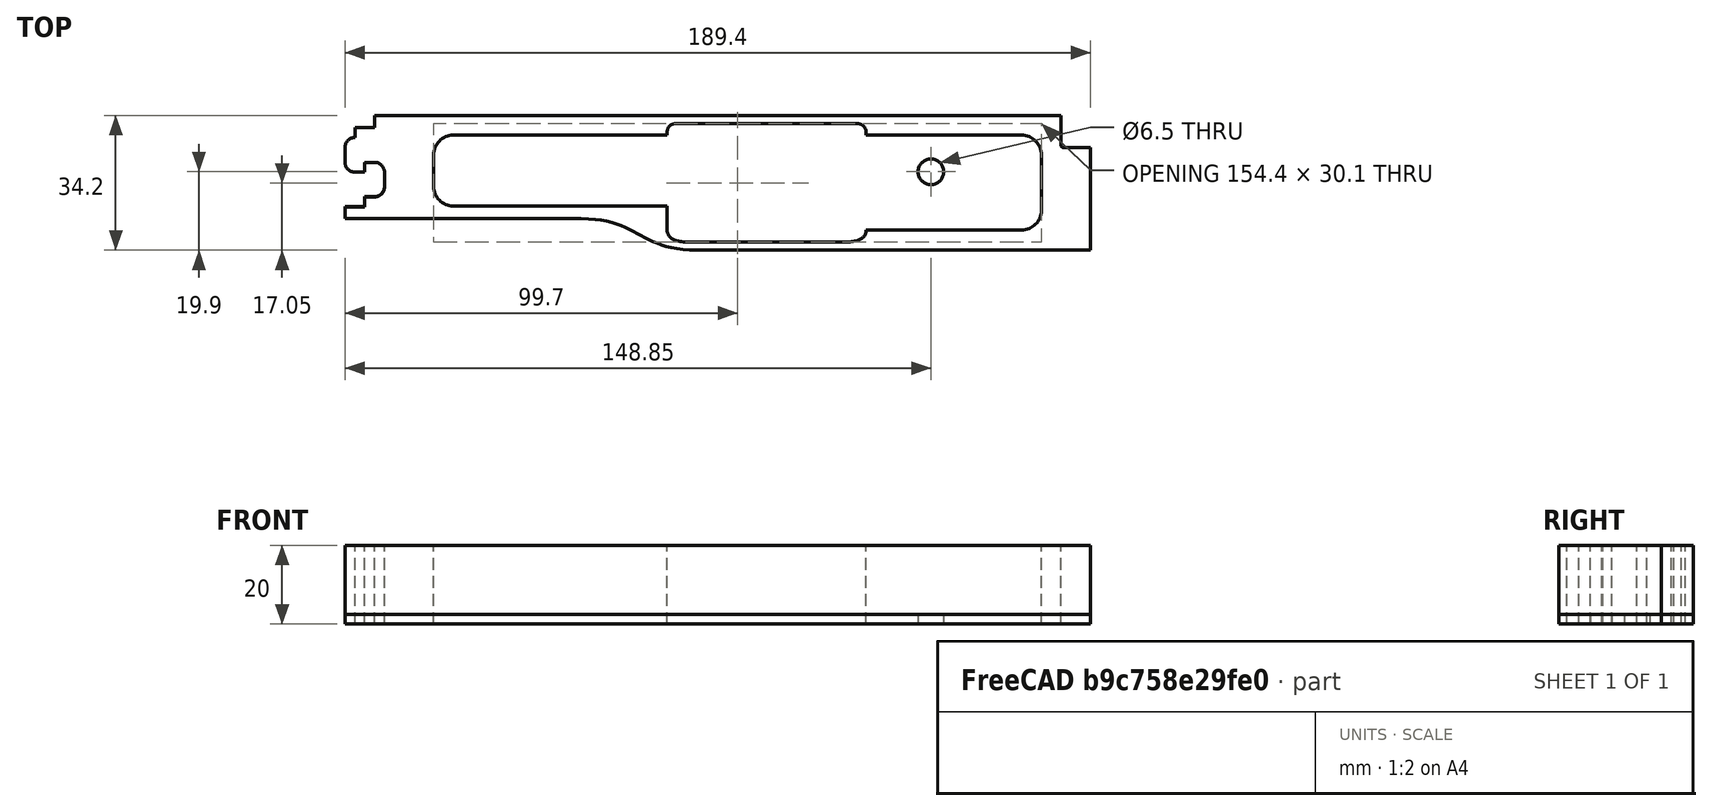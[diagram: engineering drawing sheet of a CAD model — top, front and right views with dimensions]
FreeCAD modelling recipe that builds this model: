
FCSTD DOCUMENT  (FreeCAD 0.19R0.19.2)
Label: v0_29
License: All rights reserved
LicenseURL: http://en.wikipedia.org/wiki/All_rights_reserved
objects: Sketcher::SketchObject×2, Part::Extrusion×2
note: 4 computed .brp shape members not serialized (recipe doc carries the construction recipe); baked Part::Feature solids carry a one-line shape summary decoded from their .brp

FEATURE [Sketcher::SketchObject] Sketch
  FullyConstrained = true
  sketch-geometry (35):
    g0: LineSegment StartX=0 StartY=0 StartZ=0 EndX=154.4 EndY=0 EndZ=0
    g1: LineSegment StartX=154.4 StartY=0 StartZ=0 EndX=154.4 EndY=-7.6 EndZ=0
    g2: ArcOfCircle CenterX=154.9 CenterY=-7.6 CenterZ=0 NormalX=0 NormalY=0 NormalZ=1 AngleXU=0 Radius=0.5 StartAngle=3.14159 EndAngle=4.71239
    g3: LineSegment StartX=32.5209 StartY=-26.2 StartZ=0 EndX=-7.5 EndY=-26.2 EndZ=0
    g4: LineSegment StartX=61.85 StartY=-34.2 StartZ=0 EndX=161.9 EndY=-34.2 EndZ=0
    g5: LineSegment StartX=161.9 StartY=-8.1 StartZ=0 EndX=161.9 EndY=-34.2 EndZ=0
    g6: LineSegment StartX=154.9 StartY=-8.1 StartZ=0 EndX=161.9 EndY=-8.1 EndZ=0
    g7-g11: Circle x5 (B-spline internal-alignment scaffolding for g12; pole/knot coordinates omitted)
    g12: BSplineCurve PolesCount=5 KnotsCount=3 Degree=3 IsPeriodic=0
    g13: GeomPoint X=61.85 Y=-34.2 Z=0
    g14: GeomPoint X=47.185 Y=-30.2 Z=0
    g15: GeomPoint X=32.5209 Y=-26.2 Z=0
    g16: Circle CenterX=121.35 CenterY=-14.3 CenterZ=0 NormalX=0 NormalY=0 NormalZ=1 AngleXU=0 Radius=3.25
    g17: LineSegment StartX=-7.5 StartY=-26.2 StartZ=0 EndX=-27.5 EndY=-26.2 EndZ=0
    g18: LineSegment StartX=-20 StartY=0 StartZ=0 EndX=0 EndY=0 EndZ=0
    g19: LineSegment StartX=-25 StartY=-3.1 StartZ=0 EndX=-20 EndY=-3.1 EndZ=0
    g20: LineSegment StartX=-25 StartY=-3.1 StartZ=0 EndX=-25 EndY=-5.6 EndZ=0
    g21: LineSegment StartX=-27.5 StartY=-8.1 StartZ=0 EndX=-27.5 EndY=-11.85 EndZ=0
    g22: ArcOfCircle CenterX=-25 CenterY=-8.1 CenterZ=0 NormalX=0 NormalY=0 NormalZ=1 AngleXU=0 Radius=2.5 StartAngle=1.5708 EndAngle=3.14159
    g23: LineSegment StartX=-25 StartY=-14.35 StartZ=0 EndX=-22.5 EndY=-14.35 EndZ=0
    g24: ArcOfCircle CenterX=-25 CenterY=-11.85 CenterZ=0 NormalX=0 NormalY=0 NormalZ=1 AngleXU=0 Radius=2.5 StartAngle=3.14159 EndAngle=4.71239
    g25: LineSegment StartX=-22.5 StartY=-14.35 StartZ=0 EndX=-22.5 EndY=-11.85 EndZ=0
    g26: LineSegment StartX=-22.5 StartY=-11.85 StartZ=0 EndX=-20 EndY=-11.85 EndZ=0
    g27: ArcOfCircle CenterX=-20 CenterY=-14.35 CenterZ=0 NormalX=0 NormalY=0 NormalZ=1 AngleXU=0 Radius=2.5 StartAngle=8e-16 EndAngle=1.5708
    g28: LineSegment StartX=-17.5 StartY=-14.35 StartZ=0 EndX=-17.5 EndY=-18.1 EndZ=0
    g29: ArcOfCircle CenterX=-20 CenterY=-18.1 CenterZ=0 NormalX=0 NormalY=0 NormalZ=1 AngleXU=0 Radius=2.5 StartAngle=4.71239 EndAngle=6.28319
    g30: LineSegment StartX=-22.5 StartY=-20.6 StartZ=0 EndX=-20 EndY=-20.6 EndZ=0
    g31: LineSegment StartX=-22.5 StartY=-20.6 StartZ=0 EndX=-22.5 EndY=-23.1 EndZ=0
    g32: LineSegment StartX=-27.5 StartY=-23.1 StartZ=0 EndX=-22.5 EndY=-23.1 EndZ=0
    g33: LineSegment StartX=-20 StartY=-3.1 StartZ=0 EndX=-20 EndY=0 EndZ=0
    g34: LineSegment StartX=-27.5 StartY=-23.1 StartZ=0 EndX=-27.5 EndY=-26.2 EndZ=0
  constraints (70):
    c: PointOnObject(g0,g-2)
    c: Horizontal(g0)
    c: Distance(g0) = 154.4
    c: DistanceY(g-1,g0) = 0
    c: Vertical(g1)
    c: Distance(g1) = 7.6
    c: Coincident(g1,g0)
    c: Block(g2)
    c: Horizontal(g4)
    c: Horizontal(g3)
    c: Block(g3)
    c: Block(g4)
    c: Vertical(g5)
    c: Distance(g5) = 26.1
    c: Coincident(g5,g4)
    c: Horizontal(g6)
    c: Coincident(g6,g5)
    c: Coincident(g6,g2)
    c: Distance(g6) = 7
    c: Coincident(g12,g4)
    c: Weight(g7) = 1
    c: Equal(g7, g8-g11) x4
    c: Coincident(g12,g3)
    c: InternalAlignment(g7-g11 -> g12) x5
    c: InternalAlignment(g13,g12)
    c: InternalAlignment(g14,g12)
    c: InternalAlignment(g15,g12)
    c: Block(g12)
    c: Block(g16)
    c: Coincident(g17,g3)
    c: Horizontal(g17)
    c: Distance(g17) = 20
    c: Horizontal(g18)
    c: Distance(g18) = 20
    c: Coincident(g18,g0)
    c: Horizontal(g19)
    c: Vertical(g20)
    c: Coincident(g20,g19)
    c: Vertical(g21)
    c: Coincident(g22,g20)
    c: Block(g22)
    c: Coincident(g21,g22)
    c: Horizontal(g23)
    c: Coincident(g24,g21)
    c: Block(g24)
    c: Block(g23)
    c: Vertical(g25)
    c: Coincident(g25,g23)
    c: Horizontal(g26)
    c: Coincident(g26,g25)
    c: Coincident(g27,g26)
    c: Vertical(g28)
    c: Block(g27)
    c: Coincident(g28,g27)
    c: Coincident(g29,g28)
    c: Block(g29)
    c: Horizontal(g30)
    c: Coincident(g30,g29)
    c: Vertical(g31)
    c: Coincident(g31,g30)
    c: Horizontal(g32)
    c: Coincident(g32,g31)
    c: Block(g19)
    c: Block(g32)
    c: Coincident(g33,g19)
    c: Coincident(g33,g18)
    c: Vertical(g33)
    c: Coincident(g34,g32)
    c: Coincident(g34,g17)
    c: Vertical(g34)
FEATURE [Part::Extrusion] Extrude
  Base = -> Sketch
  Dir = (0,0,1)
  DirMode = 2
  FaceMakerClass = Part::FaceMakerBullseye
  LengthFwd = 2.4
  LengthRev = 0
  Solid = true
  Symmetric = false
FEATURE [Sketcher::SketchObject] Sketch001
  FullyConstrained = true
  sketch-geometry (65):
    g0: ArcOfCircle CenterX=144.4 CenterY=-10 CenterZ=0 NormalX=0 NormalY=0 NormalZ=1 AngleXU=0 Radius=5 StartAngle=0 EndAngle=1.5708
    g1: LineSegment StartX=32.5209 StartY=-26.2 StartZ=0 EndX=-7.49911 EndY=-26.2 EndZ=0
    g2: LineSegment StartX=61.85 StartY=-34.2 StartZ=0 EndX=161.9 EndY=-34.2 EndZ=0
    g3: ArcOfCircle CenterX=144.4 CenterY=-24.1 CenterZ=0 NormalX=0 NormalY=0 NormalZ=1 AngleXU=0 Radius=5 StartAngle=4.71239 EndAngle=6.28319
    g4: Circle CenterX=104.85 CenterY=-29.2 CenterZ=0 NormalX=0 NormalY=0 NormalZ=1 AngleXU=0 Radius=1
    g5: Circle CenterX=104.85 CenterY=-32.2 CenterZ=0 NormalX=0 NormalY=0 NormalZ=1 AngleXU=0 Radius=1
    g6: Circle CenterX=98.85 CenterY=-32.2 CenterZ=0 NormalX=0 NormalY=0 NormalZ=1 AngleXU=0 Radius=1
    g7: BSplineCurve PolesCount=3 KnotsCount=2 Degree=2 IsPeriodic=0
    g8: GeomPoint X=104.85 Y=-29.2 Z=0
    g9: GeomPoint X=98.85 Y=-32.2 Z=0
    g10: Circle CenterX=54.35 CenterY=-29.2 CenterZ=0 NormalX=0 NormalY=0 NormalZ=1 AngleXU=0 Radius=1
    g11: Circle CenterX=60.35 CenterY=-32.2 CenterZ=0 NormalX=0 NormalY=0 NormalZ=1 AngleXU=0 Radius=1
    g12: BSplineCurve PolesCount=3 KnotsCount=2 Degree=2 IsPeriodic=0
    g13: GeomPoint X=54.35 Y=-29.2 Z=0
    g14: GeomPoint X=60.35 Y=-32.2 Z=0
    g15: ArcOfCircle CenterX=56.35 CenterY=-4.1 CenterZ=0 NormalX=0 NormalY=0 NormalZ=1 AngleXU=0 Radius=2 StartAngle=1.5708 EndAngle=3.14159
    g16: ArcOfCircle CenterX=102.85 CenterY=-4.1 CenterZ=0 NormalX=0 NormalY=0 NormalZ=1 AngleXU=0 Radius=2 StartAngle=1e-16 EndAngle=1.5708
    g17: LineSegment StartX=0 StartY=0 StartZ=0 EndX=154.4 EndY=0 EndZ=0
    g18: ArcOfCircle CenterX=154.9 CenterY=-7.6 CenterZ=0 NormalX=0 NormalY=0 NormalZ=1 AngleXU=0 Radius=0.5 StartAngle=3.14159 EndAngle=4.71239
    g19-g23: Circle x5 (B-spline internal-alignment scaffolding for g24; pole/knot coordinates omitted)
    g24: BSplineCurve PolesCount=5 KnotsCount=3 Degree=3 IsPeriodic=0
    g25: GeomPoint X=61.85 Y=-34.2 Z=0
    g26: GeomPoint X=47.1857 Y=-30.2 Z=0
    g27: GeomPoint X=32.5209 Y=-26.2 Z=0
    g28: LineSegment StartX=154.4 StartY=0 StartZ=0 EndX=154.4 EndY=-7.6 EndZ=0
    g29: LineSegment StartX=154.9 StartY=-8.1 StartZ=0 EndX=161.9 EndY=-8.1 EndZ=0
    g30: LineSegment StartX=161.9 StartY=-8.1 StartZ=0 EndX=161.9 EndY=-34.2 EndZ=0
    g31: LineSegment StartX=20 StartY=-5 StartZ=0 EndX=54.35 EndY=-5 EndZ=0
    g32: LineSegment StartX=54.35 StartY=-5 StartZ=0 EndX=54.35 EndY=-4.1 EndZ=0
    g33: LineSegment StartX=56.35 StartY=-2.1 StartZ=0 EndX=102.85 EndY=-2.1 EndZ=0
    g34: LineSegment StartX=104.85 StartY=-4.1 StartZ=0 EndX=104.85 EndY=-5 EndZ=0
    g35: LineSegment StartX=104.85 StartY=-5 StartZ=0 EndX=144.4 EndY=-5 EndZ=0
    g36: LineSegment StartX=149.4 StartY=-10 StartZ=0 EndX=149.4 EndY=-24.1 EndZ=0
    g37: LineSegment StartX=144.4 StartY=-29.1 StartZ=0 EndX=104.85 EndY=-29.1 EndZ=0
    g38: LineSegment StartX=104.85 StartY=-29.1 StartZ=0 EndX=104.85 EndY=-29.2 EndZ=0
    g39: LineSegment StartX=98.85 StartY=-32.2 StartZ=0 EndX=60.35 EndY=-32.2 EndZ=0
    g40: LineSegment StartX=54.35 StartY=-29.2 StartZ=0 EndX=54.35 EndY=-23 EndZ=0
    g41: LineSegment StartX=54.35 StartY=-23 StartZ=0 EndX=20 EndY=-23 EndZ=0
    g42: LineSegment StartX=-27.4991 StartY=-26.2 StartZ=0 EndX=-7.49911 EndY=-26.2 EndZ=0
    g43: LineSegment StartX=-20 StartY=0 StartZ=0 EndX=0 EndY=0 EndZ=0
    g44: LineSegment StartX=-27.4991 StartY=-23.2 StartZ=0 EndX=-22.5 EndY=-23.2 EndZ=0
    g45: LineSegment StartX=-22.5 StartY=-20.7 StartZ=0 EndX=-22.5 EndY=-23.2 EndZ=0
    g46: LineSegment StartX=-22.5 StartY=-20.7 StartZ=0 EndX=-20 EndY=-20.7 EndZ=0
    g47: ArcOfCircle CenterX=-20 CenterY=-18.2 CenterZ=0 NormalX=0 NormalY=0 NormalZ=1 AngleXU=0 Radius=2.5 StartAngle=4.71239 EndAngle=6.28319
    g48: LineSegment StartX=-17.5 StartY=-14.4 StartZ=0 EndX=-17.5 EndY=-18.2 EndZ=0
    g49: ArcOfCircle CenterX=-20 CenterY=-14.4 CenterZ=0 NormalX=0 NormalY=0 NormalZ=1 AngleXU=0 Radius=2.5 StartAngle=9e-16 EndAngle=1.5708
    g50: LineSegment StartX=-22.5 StartY=-11.9 StartZ=0 EndX=-20 EndY=-11.9 EndZ=0
    g51: LineSegment StartX=-22.5 StartY=-14.4 StartZ=0 EndX=-22.5 EndY=-11.9 EndZ=0
    g52: LineSegment StartX=-25 StartY=-14.4 StartZ=0 EndX=-22.5 EndY=-14.4 EndZ=0
    g53: ArcOfCircle CenterX=-25 CenterY=-11.9 CenterZ=0 NormalX=0 NormalY=0 NormalZ=1 AngleXU=0 Radius=2.5 StartAngle=3.14159 EndAngle=4.71239
    g54: LineSegment StartX=-27.5 StartY=-8.1 StartZ=0 EndX=-27.5 EndY=-11.9 EndZ=0
    g55: ArcOfCircle CenterX=-25 CenterY=-8.1 CenterZ=0 NormalX=0 NormalY=0 NormalZ=1 AngleXU=0 Radius=2.5 StartAngle=1.5708 EndAngle=3.14159
    g56: LineSegment StartX=-25 StartY=-3.1 StartZ=0 EndX=-25 EndY=-5.6 EndZ=0
    g57: LineSegment StartX=-20 StartY=-3.1 StartZ=0 EndX=-25 EndY=-3.1 EndZ=0
    g58: LineSegment StartX=-20 StartY=0 StartZ=0 EndX=-20 EndY=-3.1 EndZ=0
    g59: LineSegment StartX=-27.4991 StartY=-26.2 StartZ=0 EndX=-27.4991 EndY=-23.2 EndZ=0
    g60: LineSegment StartX=4.09e-14 StartY=-5 StartZ=0 EndX=20 EndY=-5 EndZ=0
    g61: ArcOfCircle CenterX=7.1e-15 CenterY=-18 CenterZ=0 NormalX=0 NormalY=0 NormalZ=1 AngleXU=0 Radius=5 StartAngle=3.14159 EndAngle=4.71239
    g62: ArcOfCircle CenterX=4.26e-14 CenterY=-10 CenterZ=0 NormalX=0 NormalY=0 NormalZ=1 AngleXU=0 Radius=5 StartAngle=1.5708 EndAngle=3.14159
    g63: LineSegment StartX=-5 StartY=-18 StartZ=0 EndX=-5 EndY=-10 EndZ=0
    g64: LineSegment StartX=0 StartY=-23 StartZ=0 EndX=20 EndY=-23 EndZ=0
  constraints (132):
    c: PointOnObject(g17,g-2)
    c: DistanceY(g-1,g17) = 0
    c: Block(g0)
    c: Horizontal(g2)
    c: Horizontal(g1)
    c: Block(g3)
    c: Distance(g1) = 40.02
    c: Weight(g4) = 1
    c: Equal(g4,g5)
    c: Equal(g4,g6)
    c: InternalAlignment(g4,g7)
    c: InternalAlignment(g5,g7)
    c: InternalAlignment(g6,g7)
    c: InternalAlignment(g8,g7)
    c: InternalAlignment(g9,g7)
    c: Block(g7)
    c: Weight(g10) = 1
    c: Equal(g10,g11)
    c: InternalAlignment(g10,g12)
    c: InternalAlignment(g11,g12)
    c: InternalAlignment(g13,g12)
    c: InternalAlignment(g14,g12)
    c: Block(g12)
    c: Block(g15)
    c: Block(g16)
    c: Horizontal(g17)
    c: Block(g2)
    c: Block(g17)
    c: Block(g18)
    c: Coincident(g24,g2)
    c: Weight(g19) = 1
    c: Equal(g19, g20-g23) x4
    c: Coincident(g24,g1)
    c: InternalAlignment(g19-g23 -> g24) x5
    c: InternalAlignment(g25,g24)
    c: InternalAlignment(g26,g24)
    c: InternalAlignment(g27,g24)
    c: Block(g24)
    c: Vertical(g28)
    c: Coincident(g28,g17)
    c: Coincident(g18,g28)
    c: Distance(g28) = 7.6
    c: Block(g28)
    c: Horizontal(g29)
    c: Coincident(g29,g18)
    c: Vertical(g30)
    c: Coincident(g30,g2)
    c: Coincident(g29,g30)
    c: Horizontal(g31)
    c: Coincident(g32,g31)
    c: Coincident(g32,g15)
    c: Vertical(g32)
    c: Coincident(g33,g15)
    c: Coincident(g33,g16)
    c: Horizontal(g33)
    c: Coincident(g34,g16)
    c: Vertical(g34)
    c: Coincident(g35,g34)
    c: Coincident(g35,g0)
    c: Horizontal(g35)
    c: Coincident(g36,g0)
    c: Coincident(g36,g3)
    c: Vertical(g36)
    c: Coincident(g37,g3)
    c: Horizontal(g37)
    c: Coincident(g38,g37)
    c: Coincident(g38,g7)
    c: Vertical(g38)
    c: Coincident(g39,g7)
    c: Coincident(g39,g12)
    c: Horizontal(g39)
    c: Coincident(g40,g12)
    c: Vertical(g40)
    c: Coincident(g41,g40)
    c: Horizontal(g41)
    c: Horizontal(g42)
    c: Distance(g42) = 20
    c: Coincident(g1,g42)
    c: Horizontal(g43)
    c: Distance(g43) = 20
    c: Coincident(g43,g17)
    c: Horizontal(g57)
    c: Vertical(g56)
    c: Coincident(g55,g56)
    c: Vertical(g54)
    c: Block(g55)
    c: Coincident(g53,g54)
    c: Block(g53)
    c: Horizontal(g52)
    c: Coincident(g52,g53)
    c: Vertical(g51)
    c: Coincident(g51,g52)
    c: Horizontal(g50)
    c: Coincident(g49,g50)
    c: Block(g49)
    c: Vertical(g48)
    c: Coincident(g47,g48)
    c: Block(g47)
    c: Horizontal(g46)
    c: Coincident(g46,g47)
    c: Vertical(g45)
    c: Coincident(g45,g46)
    c: Horizontal(g44)
    c: Coincident(g44,g45)
    c: Coincident(g58,g43)
    c: Coincident(g58,g57)
    c: Vertical(g58)
    c: Coincident(g59,g42)
    c: Coincident(g59,g44)
    c: Vertical(g59)
    c: Block(g59)
    c: Block(g44)
    c: Block(g48)
    c: Block(g52)
    c: Block(g51)
    c: Block(g50)
    c: Block(g54)
    c: Block(g57)
    c: Block(g56)
    c: Horizontal(g60)
    c: Distance(g60) = 20
    c: Block(g61)
    c: Block(g62)
    c: Coincident(g63,g61)
    c: Coincident(g63,g62)
    c: Vertical(g63)
    c: Coincident(g64,g61)
    c: Coincident(g64,g41)
    c: Horizontal(g64)
    c: Block(g64)
    c: Block(g60)
    c: Block(g31)
FEATURE [Part::Extrusion] Extrude001
  Base = -> Sketch001
  Dir = (0,0,1)
  DirMode = 2
  FaceMakerClass = Part::FaceMakerBullseye
  LengthFwd = 20
  LengthRev = 0
  Solid = true
  Symmetric = false
